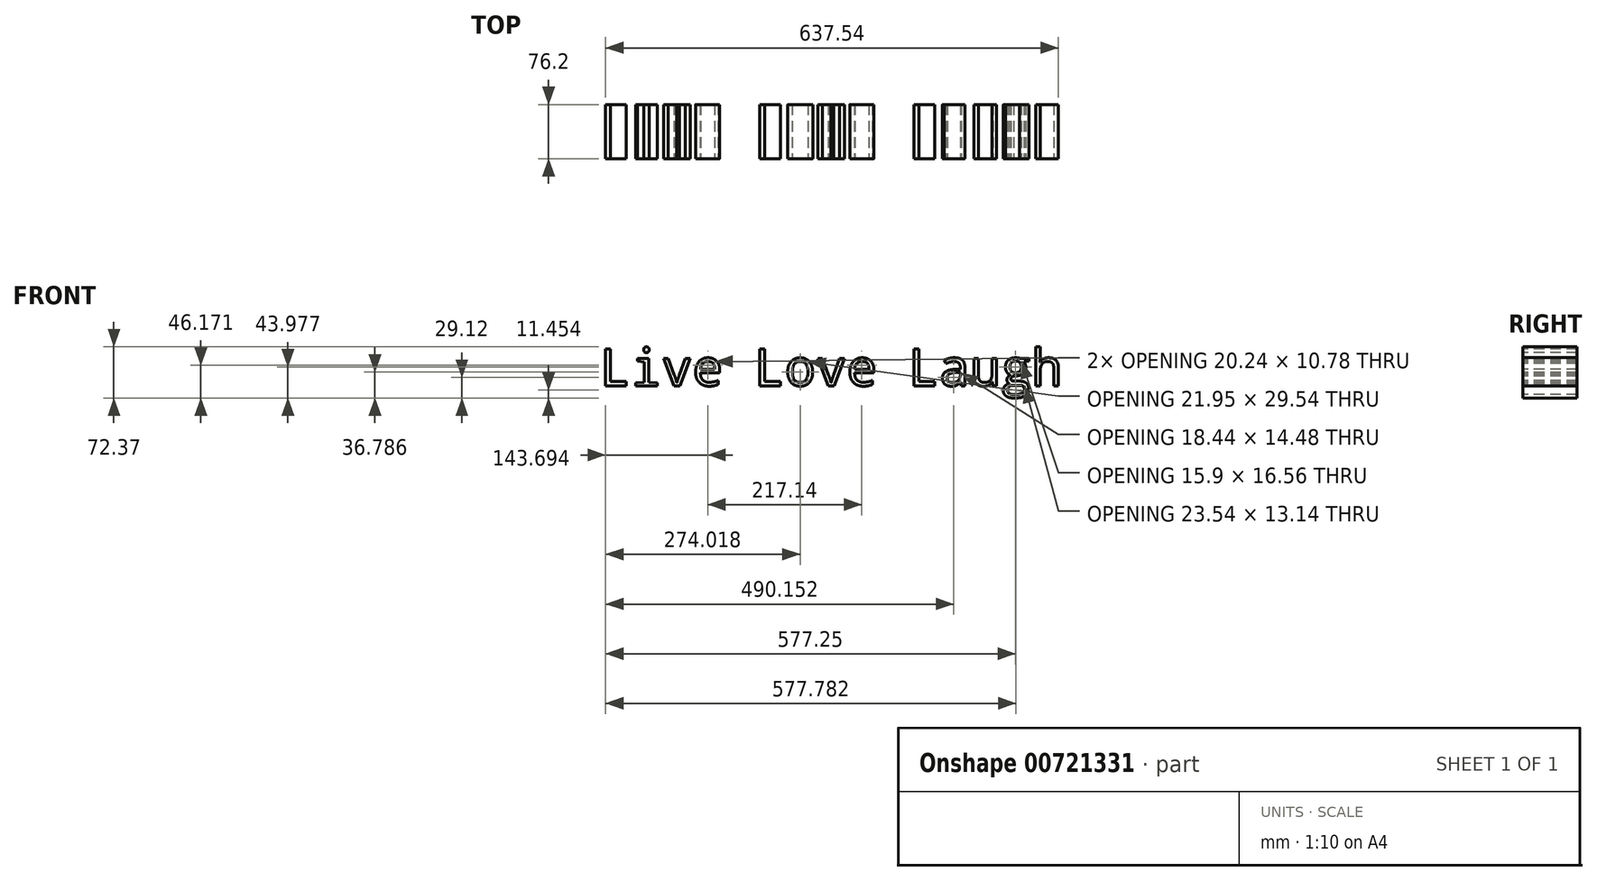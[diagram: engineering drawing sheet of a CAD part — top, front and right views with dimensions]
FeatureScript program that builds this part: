
annotation { "Feature Type Name" : "Feature", "Feature Type Description" : "" }
export const myFeature = defineFeature(function(context is Context, id is Id, definition is map)
    precondition{}
    {
        {
            var Q0;
            Q0=qCreatedBy(makeId("Front.planeOp"),FACE);
            var sketch = newSketch(context, id + "F0", { "sketchPlane" : qUnion([Q0])});
            skText(sketch, "E0", { "text": "Live Love Laugh", "fontName": "DroidSansMono.ttf"});
            const initialGuessF0  = {"E0": [-0.1192, -0.02338, 1, 0, 0.0521]};
            skSetInitialGuess(sketch, initialGuessF0);
            skSolve(sketch);
        }
        {
            var Q0;
            Q0 = qSketchRegion(id + "F0", true);
            extrude(context, id + "F1", {"entities" : qUnion([Q0]), "oppositeDirection" : true, "depth" : 76.2 * mm, "offsetDistance" : 25.4 * mm});
        }
    });
